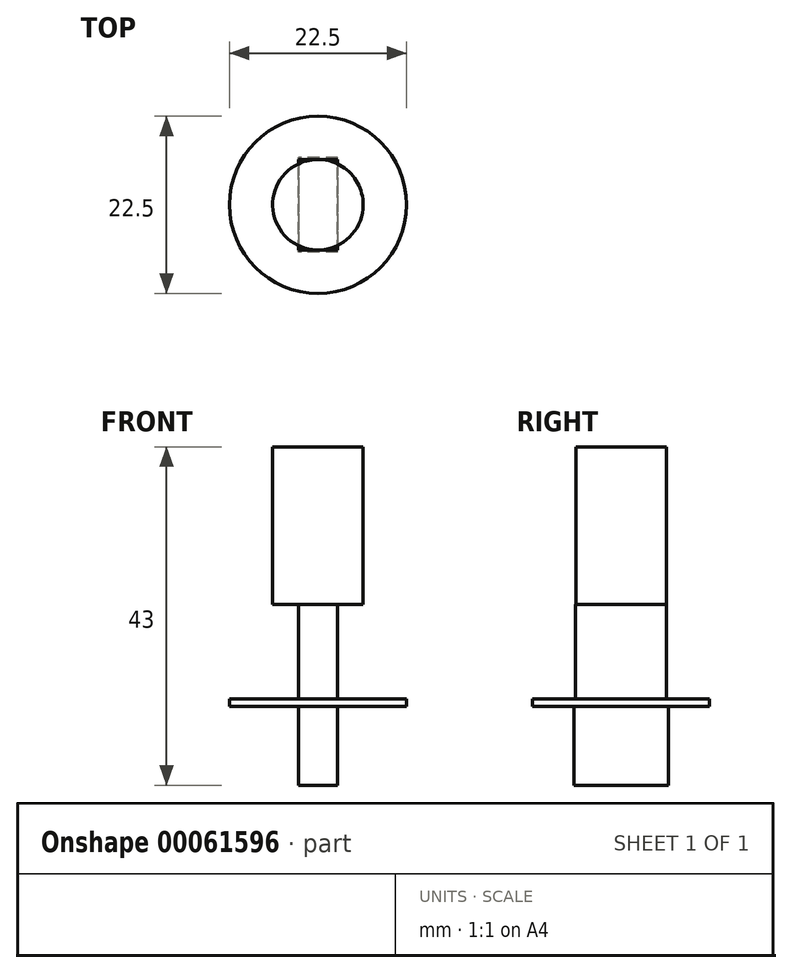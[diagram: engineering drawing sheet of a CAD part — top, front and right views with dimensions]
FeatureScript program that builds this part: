
annotation { "Feature Type Name" : "Feature", "Feature Type Description" : "" }
export const myFeature = defineFeature(function(context is Context, id is Id, definition is map)
    precondition{}
    {
        {
            var Q0;
            Q0=qCreatedBy(makeId("Top.planeOp"),FACE);
            var sketch = newSketch(context, id + "F0", { "sketchPlane" : qUnion([Q0])});
            skCircle(sketch, "E0", {"center": v(0, 0) * mm, "radius": 11.25 * mm});
            skSolve(sketch);
        }
        {
            var Q0;
            Q0 = qSketchRegion(id + "F0", true);
            extrude(context, id + "F1", {"entities" : qUnion([Q0]), "depth" : 1 * mm});
        }
        {
            var Q0;
            Q0=makeQuery(id+"F1.opExtrude","CAP_FACE",FACE,{"disambiguationData":[OSD([sQuery(id+"F0.wireOp",EDGE,"E0")])],"isStart":false});
            var sketch = newSketch(context, id + "F2", { "sketchPlane" : qUnion([Q0])});
            skLineSegment(sketch, "E1.rect.bottom", {"start": v(2.5, 5.77) * mm, "end": v(-2.5, 5.77) * mm});
            skLineSegment(sketch, "E1.rect.top", {"start": v(2.5, -5.77) * mm, "end": v(-2.5, -5.77) * mm});
            skLineSegment(sketch, "E1.rect.left", {"start": v(2.5, 5.77) * mm, "end": v(2.5, -5.77) * mm});
            skLineSegment(sketch, "E1.rect.right", {"start": v(-2.5, 5.77) * mm, "end": v(-2.5, -5.77) * mm});
            skPoint(sketch, "E1.rect.middle", {"position": v(0, 0) * mm});
            skSolve(sketch);
        }
        {
            var Q0;
            Q0 = qSketchRegion(id + "F2", true);
            extrude(context, id + "F3", {"entities" : qUnion([Q0]), "operationType" : NewBodyOperationType.ADD, "depth" : 12 * mm});
        }
        {
            var Q0;
            Q0=qCreatedBy(makeId("Top.planeOp"),FACE);
            var sketch = newSketch(context, id + "F4", { "sketchPlane" : qUnion([Q0])});
            skLineSegment(sketch, "E2.rect.bottom", {"start": v(2.5, -6) * mm, "end": v(-2.5, -6) * mm});
            skLineSegment(sketch, "E2.rect.top", {"start": v(2.5, 6) * mm, "end": v(-2.5, 6) * mm});
            skLineSegment(sketch, "E2.rect.left", {"start": v(2.5, -6) * mm, "end": v(2.5, 6) * mm});
            skLineSegment(sketch, "E2.rect.right", {"start": v(-2.5, -6) * mm, "end": v(-2.5, 6) * mm});
            skPoint(sketch, "E2.rect.middle", {"position": v(0, 0) * mm});
            skSolve(sketch);
        }
        {
            var Q0;
            Q0=makeQuery(id+"F4.imprint","IMPRINT",FACE,{"disambiguationData":[TD([[makeQuery(id+"F4.imprint","IMPRINT",EDGE,{"derivedFrom":sQuery(id+"F4.wireOp",EDGE,"E2.rect.bottom")}),-1.0]])]});
            extrude(context, id + "F5", {"entities" : qUnion([Q0]), "operationType" : NewBodyOperationType.ADD, "oppositeDirection" : true, "depth" : 10 * mm});
        }
        {
            var Q0;
            Q0=makeQuery(id+"F3.opExtrude","CAP_FACE",FACE,{"disambiguationData":[OSD([sQuery(id+"F2.wireOp",EDGE,"E1.rect.bottom"),sQuery(id+"F2.wireOp",EDGE,"E1.rect.top"),sQuery(id+"F2.wireOp",EDGE,"E1.rect.left"),sQuery(id+"F2.wireOp",EDGE,"E1.rect.right")])],"isStart":false});
            var sketch = newSketch(context, id + "F6", { "sketchPlane" : qUnion([Q0])});
            skCircle(sketch, "E3", {"center": v(0, 0) * mm, "radius": 5.75 * mm});
            skSolve(sketch);
        }
        {
            var Q0;
            {var subQ0=sQuery(id+"F6.wireOp",EDGE,"E3");var subQ1=makeQuery(id+"F3.opExtrude","CAP_EDGE",EDGE,{"disambiguationData":[OSD([sQuery(id+"F2.wireOp",EDGE,"E1.rect.right")])],"isStart":false});var subQ2=makeQuery(id+"F6.imprint","INTERSECT",VERTEX,{"disambiguationData":[OD(0.0)],"derivedFrom":[subQ1,subQ0]});Q0=makeQuery(id+"F6.imprint","IMPRINT",FACE,{"disambiguationData":[TD([[makeQuery(id+"F6.imprint","IMPRINT",EDGE,{"disambiguationData":[TD([[subQ2,-1.0]])],"derivedFrom":subQ0}),1.0]])]});}
            var Q1;
            {var subQ0=sQuery(id+"F6.wireOp",EDGE,"E3");var subQ1=makeQuery(id+"F3.opExtrude","CAP_EDGE",EDGE,{"disambiguationData":[OSD([sQuery(id+"F2.wireOp",EDGE,"E1.rect.right")])],"isStart":false});var subQ2=makeQuery(id+"F6.imprint","INTERSECT",VERTEX,{"disambiguationData":[OD(0.0)],"derivedFrom":[subQ1,subQ0]});Q1=makeQuery(id+"F6.imprint","IMPRINT",FACE,{"disambiguationData":[TD([[makeQuery(id+"F6.imprint","IMPRINT",EDGE,{"disambiguationData":[TD([[subQ2,1.0]])],"derivedFrom":subQ0}),1.0]])]});}
            var Q2;
            {var subQ0=sQuery(id+"F6.wireOp",EDGE,"E3");var subQ1=makeQuery(id+"F3.opExtrude","CAP_EDGE",EDGE,{"disambiguationData":[OSD([sQuery(id+"F2.wireOp",EDGE,"E1.rect.left")])],"isStart":false});var subQ2=makeQuery(id+"F6.imprint","INTERSECT",VERTEX,{"disambiguationData":[OD(0.0)],"derivedFrom":[subQ1,subQ0]});Q2=makeQuery(id+"F6.imprint","IMPRINT",FACE,{"disambiguationData":[TD([[makeQuery(id+"F6.imprint","IMPRINT",EDGE,{"disambiguationData":[TD([[subQ2,1.0]])],"derivedFrom":subQ0}),1.0]])]});}
            extrude(context, id + "F7", {"entities" : qUnion([Q0, Q1, Q2]), "operationType" : NewBodyOperationType.ADD, "depth" : (32 - 12) * mm});
        }
    });
